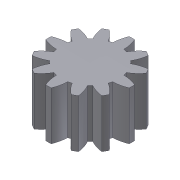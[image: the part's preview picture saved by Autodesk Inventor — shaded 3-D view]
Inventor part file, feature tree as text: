
AUTODESK INVENTOR PART (.ipt)
format: ipt  version: 2014 (Build 180170000, 170)  size: 151,040 bytes
history: native  units: mm (DEFAULTED — no unit token found)
features: plane x3, extrude x2, other x2, sketch x2
ambient origin geometry x8: Origin, YZ Plane, XZ Plane, XY Plane, X Axis, Y Axis, Z Axis, Center Point
bodies: Solid1 (feature_tree)
feature tree (9):
  extrude  "Extrusion1"  Depth=12.75mm TaperAngle=0.0deg
  plane  "Work Plane2"
  plane  "Work Plane8"
  plane  "Work Plane9"
  other  "Spur Gear"
  sketch  "Sketch1"  dims[d0=22.0mm d1=12.75mm d2=0.0mm]
  sketch  "Sketch2"  dims[d3=19.05mm d4=10.0mm d5=0.0mm d16=19.05mm d17=0.0mm d34=15.0deg d39=0.0mm d41=0.0mm d43=19.05mm d46=19.05mm d47=0.0mm d48=0.0mm]
  other  "Srf1"
  extrude  "ExtrusionSrf1"  Depth=10.0mm TaperAngle=0.0deg
